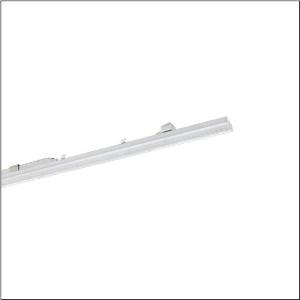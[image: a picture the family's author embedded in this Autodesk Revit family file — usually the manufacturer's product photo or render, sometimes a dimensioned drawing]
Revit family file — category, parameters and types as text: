
# Revit family: tl_l_5wd7a8f0g2c5
name_source: partatom
category: Lighting Fixtures
units: mm (PartAtom-declared; Revit-internal decimal feet)

## family parameters
Cut with Voids When Loaded = No
Host = Face
Light Source = No
Part Type = Normal
Room Calculation Point = No
Round Connector Dimension = Use Diameter
Shared = No

## types (1)
- TL L (1 x LED, 9800 lm, 63.3 W, 4000K)
    Apparent Load = 63 VA
    CIE Flux Codes = 49 84 98 100 100
    Color Rendering = 80
    Color Temperature = 4000K
    Default Elevation = 1800 mm
    Description = TL L, luminaire insert, of sheet steel, galvanised, coil coated, white, length: 1.500mm, width: 66mm, height: 67mm, surge protection,LED rated luminous flux: 9.800lm, light colour: 840, control gear: 4..20mA, with terminal, 5-pole, mains connection: 230..240V, AC, 50/60Hz, rated input power: 63W, primary optical cover: cover, of PMMA, light emission: direct distribution, protection rating (complete): as luminaire, insulation class (complete): insulation class I (protective earthing), certification: CE, impact resistance: IK06, permissible ambient temperature for indoor applications: -25..+35°C, packaging unit: 1 piece
    Height = 120 mm
    Lamp = 1 x LED
    Lamp Light Flux = 9800 lm
    Lamp Power = 63.3 W
    Lamp count = 1
    Length = 1690 mm
    Luminous efficacy = 155 lm/W
    Manufacturer = Siteco
    ModVariant = No
    Model = 5WD7A8F0G2C5
    Mounting Place = Ceiling
    Mounting Type = Pendant
    Number of Poles = 1
    OnlyDefault = Yes
    Power Factor = 1
    Product Name = TL L
    Product group = luminaire insert
    ProductGroupID = 901
    Protection Class = Protection class I
    Protection Degree = Degree of protection
    RLX_Detail_Level = 1
    RLX_Emergency_Light_Flux = 0 lm
    RLX_Emergency_Type = 0
    RLX_Emergency_Type_DB = No
    RlxData = <blob elided: 14109 chars, md5=9722f501>
    Socket = socket
    Standby Power = 0 W
    System Light Flux = 9800 lm
    System Power = 63 W
    Type Comments = Product without accessories
    Type Image = l_1294382.jpg
    URL = http://relux.com
    VarID = ---
    Voltage = 0 V
    Weight = 0.00 kg
    Width = 208 mm

## geometry (parser evidence)
native form markers: Sweep x11
no freeform markers — native parametric forms only
